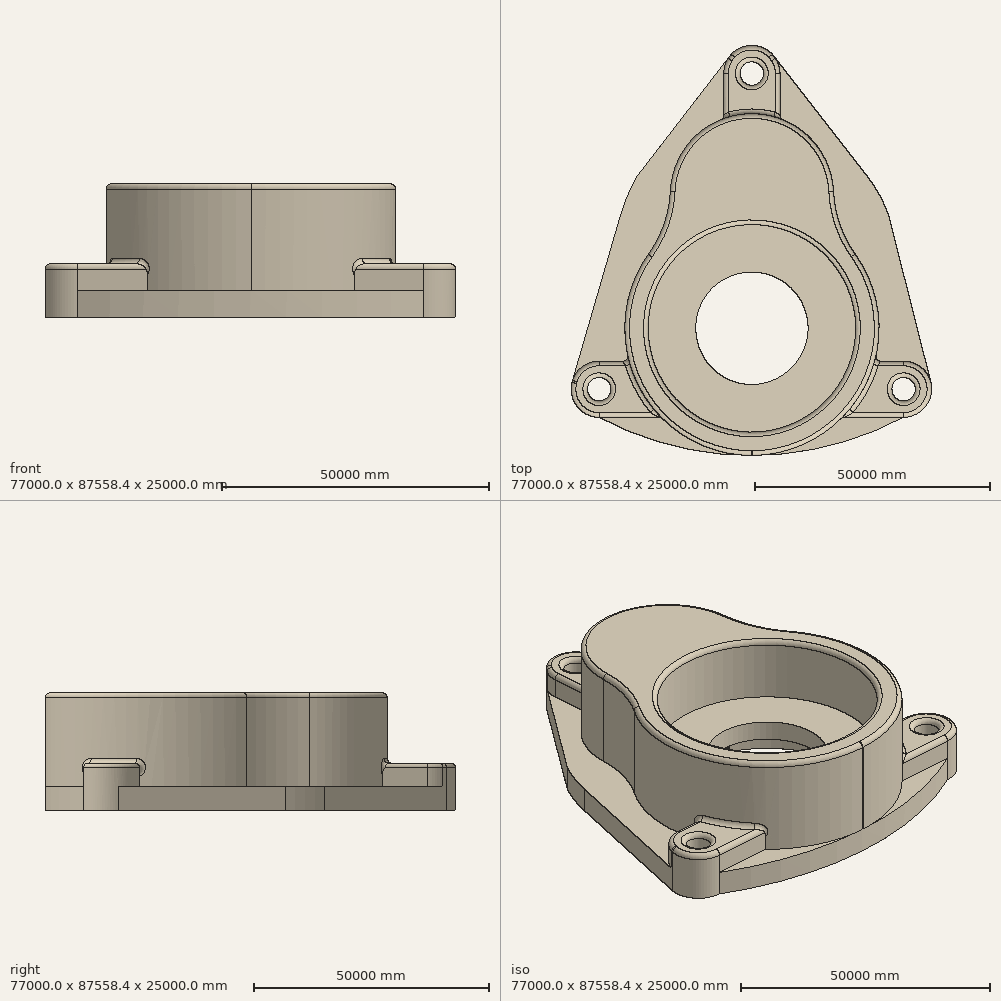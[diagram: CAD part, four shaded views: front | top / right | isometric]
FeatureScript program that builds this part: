
annotation { "Feature Type Name" : "Feature", "Feature Type Description" : "" }
export const myFeature = defineFeature(function(context is Context, id is Id, definition is map)
    precondition{}
    {
        {
            var Q0;
            Q0=qCreatedBy(makeId("Top.planeOp"),FACE);
            var sketch = newSketch(context, id + "F0", { "sketchPlane" : qUnion([Q0])});
            skCircle(sketch, "E0", {"center": v(0, 0) * mm, "radius": 22152.24 * mm});
            skCircle(sketch, "E1", {"center": v(0, 0) * mm, "radius": 12000 * mm});
            skCircle(sketch, "E2", {"center": v(0, 28406.12) * mm, "radius": 12441.64 * mm});
            skArc(sketch, "E3", {"start": v(16152.48, 21825.24) * mm, "mid": v(0, 45847.76) * mm, "end": v(-16152.48, 21825.24) * mm});
            skCircle(sketch, "E4", {"center": v(32402.2, -13014.05) * mm, "radius": 6000 * mm});
            skLineSegment(sketch, "E5", {"start": v(32402.2, -7014.05) * mm, "end": v(26230.65, -7014.05) * mm});
            skLineSegment(sketch, "E6", {"start": v(32402.2, -19014.05) * mm, "end": v(19121.28, -19014.05) * mm});
            skCircle(sketch, "E7", {"center": v(32402.2, -13014.05) * mm, "radius": 2500 * mm});
            skCircle(sketch, "E8", {"center": v(0, 54406.12) * mm, "radius": 6000 * mm});
            skLineSegment(sketch, "E9", {"start": v(6000, 54406.12) * mm, "end": v(6000, 44783.27) * mm});
            skLineSegment(sketch, "E10", {"start": v(-6000, 54406.12) * mm, "end": v(-6000, 44783.27) * mm});
            skCircle(sketch, "E11", {"center": v(0, 54406.12) * mm, "radius": 2500 * mm});
            skCircle(sketch, "E12", {"center": v(-32597.8, -13014.05) * mm, "radius": 6000 * mm});
            skLineSegment(sketch, "E13", {"start": v(-32597.8, -19014.05) * mm, "end": v(-19383.24, -19014.05) * mm});
            skCircle(sketch, "E14", {"center": v(-32597.8, -13014.05) * mm, "radius": 2500 * mm});
            skLineSegment(sketch, "E15", {"start": v(-32597.8, -7014.05) * mm, "end": v(-26230.65, -7014.05) * mm});
            skArc(sketch, "E16", {"start": v(-16152.48, 21825.24) * mm, "mid": v(0, 27152.24) * mm, "end": v(16152.48, 21825.24) * mm, "construction": true});
            skArc(sketch, "E17", {"start": v(-16152.48, 21825.24) * mm, "mid": v(0, -27152.24) * mm, "end": v(16152.48, 21825.24) * mm});
            skLineSegment(sketch, "E18", {"start": v(0, 0) * mm, "end": v(0, 27152.24) * mm, "construction": true});
            skPoint(sketch, "E19", {"position": v(-4420.45, 18433.98) * mm});
            skPoint(sketch, "E20", {"position": v(4729.52, 18433.98) * mm});
            skLineSegment(sketch, "E21", {"start": v(-27345.47, 28406.12) * mm, "end": v(27654.53, 28406.12) * mm, "construction": true});
            skLineSegment(sketch, "E22", {"start": v(-38414.37, -11541.79) * mm, "end": v(-28077.36, 24046.28) * mm});
            skLineSegment(sketch, "E23", {"start": v(38218.77, -11541.79) * mm, "end": v(29210.88, 24046.28) * mm});
            skLineSegment(sketch, "E24", {"start": v(-4409.56, 58475) * mm, "end": v(-24512.83, 32395.19) * mm});
            skLineSegment(sketch, "E25", {"start": v(4409.56, 58475) * mm, "end": v(24677.59, 32395.19) * mm});
            skArc(sketch, "E26", {"start": v(29210.88, 24046.28) * mm, "mid": v(27285.66, 28406.12) * mm, "end": v(24677.59, 32395.19) * mm});
            skArc(sketch, "E27", {"start": v(-24512.83, 32395.19) * mm, "mid": v(-26547.61, 28328.55) * mm, "end": v(-28077.36, 24046.28) * mm});
            skPoint(sketch, "E28", {"position": v(0, -27152.24) * mm});
            skArc(sketch, "E29", {"start": v(-32597.8, -19014.05) * mm, "mid": v(-97.8, -27152.3) * mm, "end": v(32402.2, -19014.05) * mm});
            skPoint(sketch, "E30", {"position": v(0, -11593.88) * mm});
            skPoint(sketch, "E31", {"position": v(27285.66, 28406.12) * mm});
            skSolve(sketch);
        }
        {
            var Q0;
            {var subQ12=sQuery(id+"F0.wireOp",EDGE,"E2");var subQ13=sQuery(id+"F0.wireOp",EDGE,"E0");var subQ14=makeQuery(id+"F0.imprint","INTERSECT",VERTEX,{"disambiguationData":[OD(0.0)],"derivedFrom":[subQ13,subQ12]});Q0=makeQuery(id+"F0.imprint","IMPRINT",FACE,{"disambiguationData":[TD([[makeQuery(id+"F0.imprint","IMPRINT",EDGE,{"disambiguationData":[TD([[subQ14,-1.0]])],"derivedFrom":subQ13}),-1.0]])]});}
            var Q1;
            {var subQ0=sQuery(id+"F0.wireOp",EDGE,"E2");var subQ1=sQuery(id+"F0.wireOp",EDGE,"E0");var subQ2=makeQuery(id+"F0.imprint","INTERSECT",VERTEX,{"disambiguationData":[OD(0.0)],"derivedFrom":[subQ1,subQ0]});Q1=makeQuery(id+"F0.imprint","IMPRINT",FACE,{"disambiguationData":[TD([[makeQuery(id+"F0.imprint","IMPRINT",EDGE,{"disambiguationData":[TD([[subQ2,1.0]])],"derivedFrom":subQ1}),-1.0]])]});}
            var Q2;
            {var subQ0=sQuery(id+"F0.wireOp",EDGE,"E2");var subQ1=sQuery(id+"F0.wireOp",EDGE,"E0");var subQ2=makeQuery(id+"F0.imprint","INTERSECT",VERTEX,{"disambiguationData":[OD(0.0)],"derivedFrom":[subQ1,subQ0]});Q2=makeQuery(id+"F0.imprint","IMPRINT",FACE,{"disambiguationData":[TD([[makeQuery(id+"F0.imprint","IMPRINT",EDGE,{"disambiguationData":[TD([[subQ2,1.0]])],"derivedFrom":subQ1}),1.0]])]});}
            var Q3;
            Q3=makeQuery(id+"F0.imprint","IMPRINT",FACE,{"disambiguationData":[TD([[makeQuery(id+"F0.imprint","IMPRINT",EDGE,{"derivedFrom":sQuery(id+"F0.wireOp",EDGE,"E1")}),-1.0]])]});
            var Q4;
            Q4=makeQuery(id+"F0.imprint","IMPRINT",FACE,{"disambiguationData":[TD([[makeQuery(id+"F0.imprint","IMPRINT",EDGE,{"derivedFrom":sQuery(id+"F0.wireOp",EDGE,"E1")}),1.0]])]});
            extrude(context, id + "F1", {"entities" : qUnion([Q0, Q1, Q2, Q3, Q4]), "depth" : 25000 * mm});
        }
        {
            var Q0;
            {var subQ0=sQuery(id+"F0.wireOp",EDGE,"E17");var subQ1=sQuery(id+"F0.wireOp",EDGE,"E3");Q0=makeQuery(id+"F1.opExtrude","SWEPT_EDGE",EDGE,{"disambiguationData":[OSD([subQ1,subQ0]),TDD([makeQuery(id+"F0.imprint","INTERSECT",VERTEX,{"disambiguationData":[OD(1.0)],"derivedFrom":[subQ1,subQ0]})])]});}
            var Q1;
            {var subQ0=sQuery(id+"F0.wireOp",EDGE,"E17");var subQ1=sQuery(id+"F0.wireOp",EDGE,"E3");Q1=makeQuery(id+"F1.opExtrude","SWEPT_EDGE",EDGE,{"disambiguationData":[OSD([subQ1,subQ0]),TDD([makeQuery(id+"F0.imprint","INTERSECT",VERTEX,{"disambiguationData":[OD(0.0)],"derivedFrom":[subQ1,subQ0]})])]});}
            fillet(context, id + "F2", {"entities" : qUnion([Q0, Q1]), "radius" : 25000 * mm, "tangentPropagation" : true, "allowEdgeOverflow" : false});
        }
        {
            var Q0;
            Q0=makeQuery(id+"F0.imprint","IMPRINT",FACE,{"disambiguationData":[TD([[makeQuery(id+"F0.imprint","IMPRINT",EDGE,{"derivedFrom":sQuery(id+"F0.wireOp",EDGE,"E11")}),-1.0]])]});
            var Q1;
            {var subQ0=sQuery(id+"F0.wireOp",EDGE,"E10");Q1=makeQuery(id+"F0.imprint","IMPRINT",FACE,{"disambiguationData":[TD([[makeQuery(id+"F0.imprint","IMPRINT",EDGE,{"derivedFrom":subQ0}),1.0]])]});}
            var Q2;
            {var subQ0=sQuery(id+"F0.wireOp",EDGE,"E9");Q2=makeQuery(id+"F0.imprint","IMPRINT",FACE,{"disambiguationData":[TD([[makeQuery(id+"F0.imprint","IMPRINT",EDGE,{"derivedFrom":subQ0}),-1.0]])]});}
            var Q3;
            Q3=makeQuery(id+"F0.imprint","IMPRINT",FACE,{"disambiguationData":[TD([[makeQuery(id+"F0.imprint","IMPRINT",EDGE,{"derivedFrom":sQuery(id+"F0.wireOp",EDGE,"E7")}),-1.0]])]});
            var Q4;
            {var subQ0=sQuery(id+"F0.wireOp",EDGE,"E5");Q4=makeQuery(id+"F0.imprint","IMPRINT",FACE,{"disambiguationData":[TD([[makeQuery(id+"F0.imprint","IMPRINT",EDGE,{"derivedFrom":subQ0}),1.0]])]});}
            var Q5;
            {var subQ3=sQuery(id+"F0.wireOp",EDGE,"E13");Q5=makeQuery(id+"F0.imprint","IMPRINT",FACE,{"disambiguationData":[TD([[makeQuery(id+"F0.imprint","IMPRINT",EDGE,{"derivedFrom":subQ3}),1.0]])]});}
            var Q6;
            Q6=makeQuery(id+"F0.imprint","IMPRINT",FACE,{"disambiguationData":[TD([[makeQuery(id+"F0.imprint","IMPRINT",EDGE,{"derivedFrom":sQuery(id+"F0.wireOp",EDGE,"E14")}),-1.0]])]});
            extrude(context, id + "F3", {"entities" : qUnion([Q0, Q1, Q2, Q3, Q4, Q5, Q6]), "operationType" : NewBodyOperationType.ADD, "depth" : 10000 * mm});
        }
        {
            var Q0;
            {var subQ0=sQuery(id+"F0.wireOp",EDGE,"E10");Q0=makeQuery(id+"F0.imprint","IMPRINT",FACE,{"disambiguationData":[TD([[makeQuery(id+"F0.imprint","IMPRINT",EDGE,{"derivedFrom":subQ0}),-1.0]])]});}
            var Q1;
            {var subQ0=sQuery(id+"F0.wireOp",EDGE,"E5");Q1=makeQuery(id+"F0.imprint","IMPRINT",FACE,{"disambiguationData":[TD([[makeQuery(id+"F0.imprint","IMPRINT",EDGE,{"derivedFrom":subQ0}),-1.0]])]});}
            var Q2;
            {var subQ0=sQuery(id+"F0.wireOp",EDGE,"E6");Q2=makeQuery(id+"F0.imprint","IMPRINT",FACE,{"disambiguationData":[TD([[makeQuery(id+"F0.imprint","IMPRINT",EDGE,{"derivedFrom":subQ0}),1.0]])]});}
            var Q3;
            {var subQ0=sQuery(id+"F0.wireOp",EDGE,"E13");Q3=makeQuery(id+"F0.imprint","IMPRINT",FACE,{"disambiguationData":[TD([[makeQuery(id+"F0.imprint","IMPRINT",EDGE,{"derivedFrom":subQ0}),-1.0]])]});}
            extrude(context, id + "F4", {"entities" : qUnion([Q0, Q1, Q2, Q3]), "operationType" : NewBodyOperationType.ADD, "depth" : 5000 * mm});
        }
        {
            var Q0;
            {var subQ0=sQuery(id+"F0.wireOp",EDGE,"E2");var subQ1=sQuery(id+"F0.wireOp",EDGE,"kqsR5tQf-KsV5-vQtr-1hwl-pM2CjywLx7pH");var subQ2=makeQuery(id+"F0.imprint","INTERSECT",VERTEX,{"disambiguationData":[OD(0.0)],"derivedFrom":[subQ1,subQ0]});Q0=makeQuery(id+"F0.imprint","IMPRINT",FACE,{"disambiguationData":[TD([[makeQuery(id+"F0.imprint","IMPRINT",EDGE,{"disambiguationData":[TD([[subQ2,-1.0]])],"derivedFrom":subQ1}),-1.0]])]});}
            var Q1;
            {var subQ0=sQuery(id+"F0.wireOp",EDGE,"E2");var subQ1=sQuery(id+"F0.wireOp",EDGE,"E0");var subQ2=makeQuery(id+"F0.imprint","INTERSECT",VERTEX,{"disambiguationData":[OD(0.0)],"derivedFrom":[subQ1,subQ0]});Q1=makeQuery(id+"F0.imprint","IMPRINT",FACE,{"disambiguationData":[TD([[makeQuery(id+"F0.imprint","IMPRINT",EDGE,{"disambiguationData":[TD([[subQ2,1.0]])],"derivedFrom":subQ1}),-1.0]])]});}
            var Q2;
            {var subQ0=sQuery(id+"F0.wireOp",EDGE,"E2");var subQ1=sQuery(id+"F0.wireOp",EDGE,"E0");var subQ2=makeQuery(id+"F0.imprint","INTERSECT",VERTEX,{"disambiguationData":[OD(0.0)],"derivedFrom":[subQ1,subQ0]});Q2=makeQuery(id+"F0.imprint","IMPRINT",FACE,{"disambiguationData":[TD([[makeQuery(id+"F0.imprint","IMPRINT",EDGE,{"disambiguationData":[TD([[subQ2,1.0]])],"derivedFrom":subQ1}),1.0]])]});}
            var Q3;
            {var subQ4=sQuery(id+"F0.wireOp",EDGE,"E1");Q3=makeQuery(id+"F0.imprint","IMPRINT",FACE,{"disambiguationData":[TD([[makeQuery(id+"F0.imprint","IMPRINT",EDGE,{"derivedFrom":subQ4}),-1.0]])]});}
            var Q4;
            Q4=makeQuery(id+"F0.imprint","IMPRINT",FACE,{"disambiguationData":[TD([[makeQuery(id+"F0.imprint","IMPRINT",EDGE,{"derivedFrom":sQuery(id+"F0.wireOp",EDGE,"E1")}),1.0]])]});
            extrude(context, id + "F5", {"entities" : qUnion([Q0, Q1, Q2, Q3, Q4]), "operationType" : NewBodyOperationType.REMOVE, "depth" : 8000 * mm});
        }
        {
            var Q0;
            Q0=makeQuery(id+"F1.opExtrude","CAP_FACE",FACE,{"disambiguationData":[OSD([sQuery(id+"F0.wireOp",EDGE,"kqsR5tQf-KsV5-vQtr-1hwl-pM2CjywLx7pH"),sQuery(id+"F0.wireOp",EDGE,"E3"),sQuery(id+"F0.wireOp",EDGE,"iEIuPQZy-EICV-oZXC-Luwi-EC5yGCYxkAy4")])],"isStart":false});
            var sketch = newSketch(context, id + "F6", { "sketchPlane" : qUnion([Q0])});
            skCircle(sketch, "E32.0", {"center": v(0, 0) * mm, "radius": 22152.24 * mm});
            skSolve(sketch);
        }
        {
            var Q0;
            Q0 = qSketchRegion(id + "F6", true);
            extrude(context, id + "F7", {"entities" : qUnion([Q0]), "operationType" : NewBodyOperationType.REMOVE, "oppositeDirection" : true, "depth" : 13000 * mm});
        }
        {
            var Q0;
            Q0=makeQuery(id+"F0.imprint","IMPRINT",FACE,{"disambiguationData":[TD([[makeQuery(id+"F0.imprint","IMPRINT",EDGE,{"derivedFrom":sQuery(id+"F0.wireOp",EDGE,"E1")}),1.0]])]});
            extrude(context, id + "F8", {"entities" : qUnion([Q0]), "operationType" : NewBodyOperationType.REMOVE, "endBound" : BoundingType.THROUGH_ALL, "depth" : 25 * mm});
        }
        {
            var Q0;
            Q0=makeQuery(id+"F1.opExtrude","CAP_FACE",FACE,{"disambiguationData":[OSD([sQuery(id+"F0.wireOp",EDGE,"E3"),sQuery(id+"F0.wireOp",EDGE,"E17"),sQuery(id+"F0.wireOp",EDGE,"E29")])],"isStart":false});
            var Q1;
            Q1=makeQuery(id+"F3.opExtrude","CAP_FACE",FACE,{"disambiguationData":[OSD([sQuery(id+"F0.wireOp",EDGE,"E4"),sQuery(id+"F0.wireOp",EDGE,"E5"),sQuery(id+"F0.wireOp",EDGE,"E6"),sQuery(id+"F0.wireOp",EDGE,"E7"),sQuery(id+"F0.wireOp",EDGE,"E17")])],"isStart":false});
            var Q2;
            Q2=makeQuery(id+"F3.opExtrude","CAP_FACE",FACE,{"disambiguationData":[OSD([sQuery(id+"F0.wireOp",EDGE,"E3"),sQuery(id+"F0.wireOp",EDGE,"E8"),sQuery(id+"F0.wireOp",EDGE,"E9"),sQuery(id+"F0.wireOp",EDGE,"E10"),sQuery(id+"F0.wireOp",EDGE,"E11"),sQuery(id+"F0.wireOp",EDGE,"E24"),sQuery(id+"F0.wireOp",EDGE,"E25")])],"isStart":false});
            var Q3;
            Q3=makeQuery(id+"F3.opExtrude","CAP_FACE",FACE,{"disambiguationData":[OSD([sQuery(id+"F0.wireOp",EDGE,"E12"),sQuery(id+"F0.wireOp",EDGE,"E13"),sQuery(id+"F0.wireOp",EDGE,"E14"),sQuery(id+"F0.wireOp",EDGE,"E15"),sQuery(id+"F0.wireOp",EDGE,"E17")])],"isStart":false});
            fillet(context, id + "F9", {"entities" : qUnion([Q0, Q1, Q2, Q3]), "radius" : 1000 * mm, "tangentPropagation" : true, "allowEdgeOverflow" : false});
        }
    });
